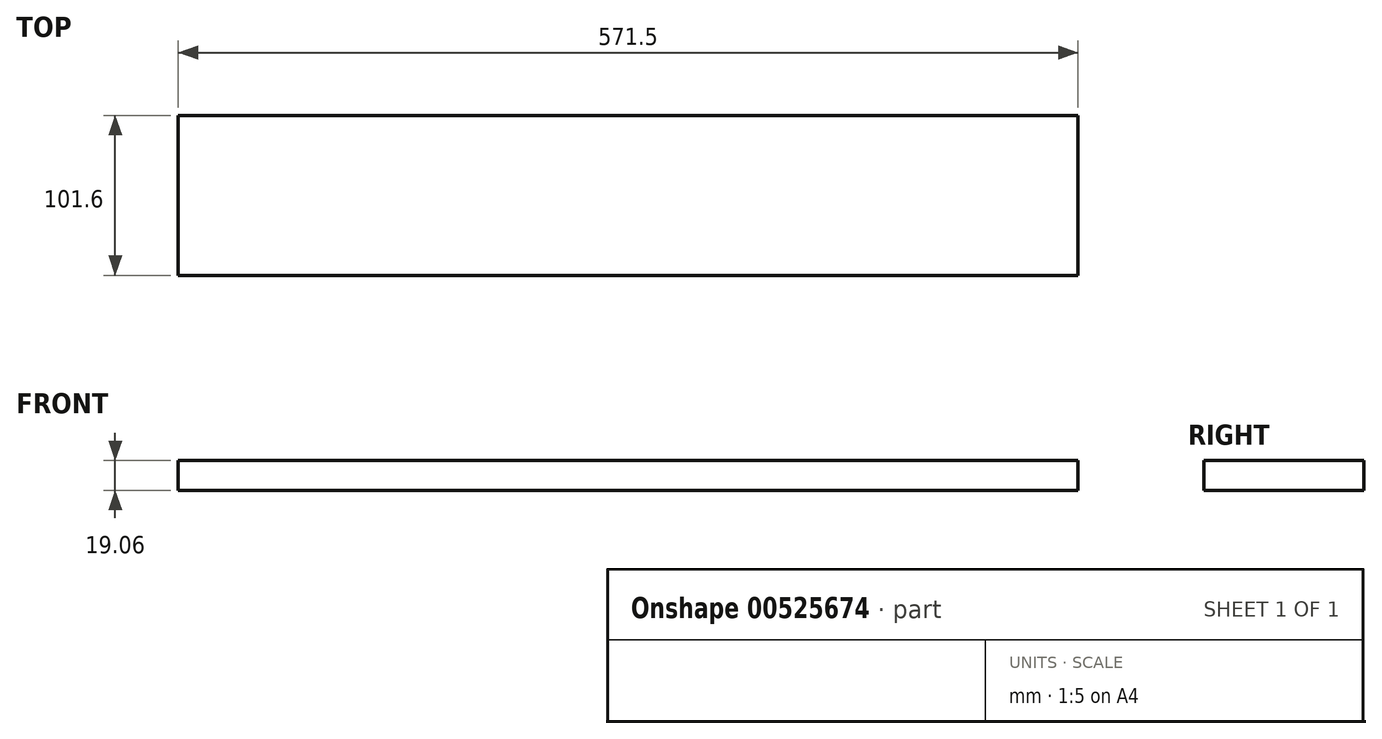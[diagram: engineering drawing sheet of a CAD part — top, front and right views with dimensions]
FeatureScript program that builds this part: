
annotation { "Feature Type Name" : "Feature", "Feature Type Description" : "" }
export const myFeature = defineFeature(function(context is Context, id is Id, definition is map)
    precondition{}
    {
        {
            var Q0;
            Q0=qCreatedBy(makeId("Top.planeOp"),FACE);
            var sketch = newSketch(context, id + "F0", { "sketchPlane" : qUnion([Q0])});
            skLineSegment(sketch, "E0.bottom", {"start": v(285.75, 50.8) * mm, "end": v(-285.75, 50.8) * mm});
            skLineSegment(sketch, "E0.top", {"start": v(285.75, -50.8) * mm, "end": v(-285.75, -50.8) * mm});
            skLineSegment(sketch, "E0.left", {"start": v(285.75, 50.8) * mm, "end": v(285.75, -50.8) * mm});
            skLineSegment(sketch, "E0.right", {"start": v(-285.75, 50.8) * mm, "end": v(-285.75, -50.8) * mm});
            skPoint(sketch, "E0.middle", {"position": v(0, 0) * mm});
            skSolve(sketch);
        }
        {
            var Q0;
            Q0 = qSketchRegion(id + "F0", true);
            extrude(context, id + "F1", {"entities" : qUnion([Q0]), "endBound" : BoundingType.SYMMETRIC, "depth" : 19.05 * mm, "offsetDistance" : 25.4 * mm});
        }
    });
